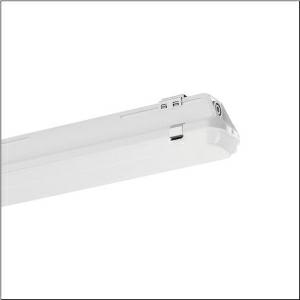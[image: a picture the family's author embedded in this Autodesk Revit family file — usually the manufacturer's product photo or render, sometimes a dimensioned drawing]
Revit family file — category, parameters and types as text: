
# Revit family: monsun_11_51fp10dp4b0u007
name_source: partatom
category: Lighting Fixtures
units: mm (PartAtom-declared; Revit-internal decimal feet)

## family parameters
Cut with Voids When Loaded = No
Host = Face
Light Source = No
Part Type = Normal
Room Calculation Point = No
Round Connector Dimension = Use Diameter
Shared = No

## types (1)
- --- (1 x LED, 12110 lm, 63.7 W, 4000K)
    Apparent Load = 64 VA
    CIE Flux Codes = 47 76 93 94 100
    Color Rendering = 80
    Color Temperature = 4000K
    Default Elevation = 1800 mm
    Description = Monsun 11, damp-proof luminaire, chain hanger, primary optical cover: enclosure, of PMMA, light emission: direct distribution, primary light characteristic: symmetric, installation type: suspended mounting, surface-mounted, horizontal mounting, vertical mounting, LED, rated luminous flux: 12.110lm, luminous efficacy: 190lm/W, light colour: 840, colour temperature: 4000K, control gear: DALI 2, with terminal, 5-pole, max. 2.5mm², through-wiring: 7x 2.5mm², mains connection: 220..240V, AC, 50/60Hz, rated input power: 64W, housing, of glass-fibre reinforced polyester, uncoated, bright grey, incl. chain hanger, length: 1.590mm, width: 90mm, height: 88mm, clip for enclosure, of stainless steel (V2A), ceiling mounting element, of stainless steel (V2A), chain hanger, of stainless steel (V2A), protection rating (complete): IP66, insulation class (complete): insulation class I (protective earthing), certification: CE, ENEC, VDE, UKCA, protection symbol: D, impact resistance: IK04, permissible operating ambient temperature: -40..+30°C, standard: EN 50419, EN 60598-2-1, corresponds to IFS (International Featured Standards) requirements for safety and quality in the food industry, for indoor or canopied outdoor use, no direct snow, no direct sun, no direct rain, LABS conformity tested according to VDMA 24364:2018-05, contact your sales advisor before using the luminaires in applications with unclear chemical exposure, large temperature fluctuations or condensation-forming humidity, packaging unit: 1 piece
    Height = 89 mm
    Lamp = 1 x LED
    Lamp Light Flux = 12110 lm
    Lamp Power = 63.7 W
    Lamp count = 1
    Length = 1590 mm
    Luminous efficacy = 190 lm/W
    Manufacturer = Siteco
    ModVariant = No
    Model = 51FP10DP4B0U007
    Mounting Place = Ceiling
    Mounting Type = Surface mounted
    Number of Poles = 1
    OnlyDefault = Yes
    Power Factor = 1
    Product Name = Monsun 11
    Product group = damp-proof luminaire
    ProductGroupID = 300
    Protection Class = Protection class I
    Protection Degree = IP 66
    RLX_Detail_Level = 1
    RLX_Emergency_Light_Flux = 0 lm
    RLX_Emergency_Type = 0
    RLX_Emergency_Type_DB = No
    RlxData = <blob elided: 92525 chars, md5=4506c67c>
    Socket = socket
    Standby Power = 0 W
    System Light Flux = 12110 lm
    System Power = 64 W
    Type Comments = factory setting: luminous flux: 100 % | dim-lin: 254 | 441 mA
    Type Image = l_1349237.jpg
    URL = http://relux.com
    VarID = @adj_037933
    Voltage = 0 V
    Weight = 0.00 kg
    Width = 90 mm

## geometry (parser evidence)
native form markers: Blend x4, Sweep x13
no freeform markers — native parametric forms only
